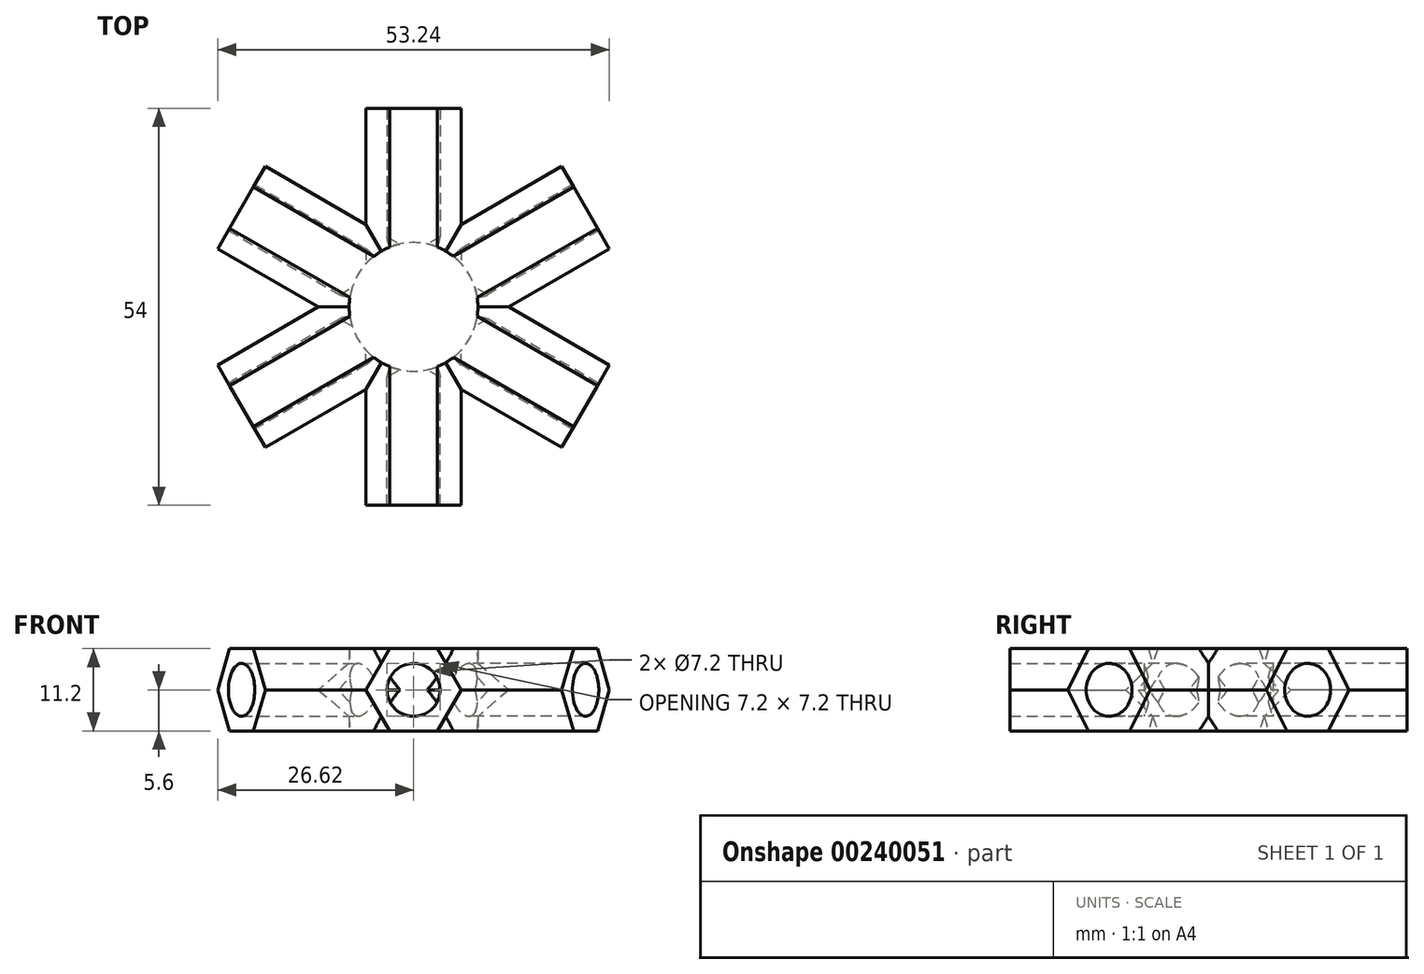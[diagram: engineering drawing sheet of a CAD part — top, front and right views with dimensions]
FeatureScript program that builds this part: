
annotation { "Feature Type Name" : "Feature", "Feature Type Description" : "" }
export const myFeature = defineFeature(function(context is Context, id is Id, definition is map)
    precondition{}
    {
        {
            var Q0;
            Q0=qCreatedBy(makeId("Front.planeOp"),FACE);
            var sketch = newSketch(context, id + "F0", { "sketchPlane" : qUnion([Q0])});
            skCircle(sketch, "E0", {"center": v(0, 0) * mm, "radius": 3.6 * mm});
            skLineSegment(sketch, "E1", {"start": v(0, 0) * mm, "end": v(0, 28.88) * mm, "construction": true});
            skLineSegment(sketch, "E2.0", {"start": v(3.23, -5.6) * mm, "end": v(-3.23, -5.6) * mm});
            skLineSegment(sketch, "E2.1", {"start": v(-3.23, -5.6) * mm, "end": v(-6.47, 0) * mm});
            skLineSegment(sketch, "E2.2", {"start": v(-6.47, 0) * mm, "end": v(-3.23, 5.6) * mm});
            skLineSegment(sketch, "E2.3", {"start": v(-3.23, 5.6) * mm, "end": v(3.23, 5.6) * mm});
            skLineSegment(sketch, "E2.4", {"start": v(3.23, 5.6) * mm, "end": v(6.47, 0) * mm});
            skLineSegment(sketch, "E2.5", {"start": v(6.47, 0) * mm, "end": v(3.23, -5.6) * mm});
            skPoint(sketch, "E2.0.midPoint", {"position": v(0, -5.6) * mm});
            skSolve(sketch);
        }
        {
            var Q0;
            Q0=makeQuery(id+"F0.imprint","IMPRINT",FACE,{"disambiguationData":[TD([[makeQuery(id+"F0.imprint","IMPRINT",EDGE,{"derivedFrom":sQuery(id+"F0.wireOp",EDGE,"E0")}),-1.0]])]});
            extrude(context, id + "F1", {"entities" : qUnion([Q0]), "depth" : 27 * mm});
        }
        {
            var Q0;
            Q0=makeQuery(id+"F1.opExtrude","SWEPT_BODY",BODY,{"disambiguationData":[OSD([sQuery(id+"F0.wireOp",EDGE,"E0"),sQuery(id+"F0.wireOp",EDGE,"0ab11b23-3792-4030-9bdc-7616e1c06152.0")])]});
            var Q1;
            Q1=sQuery(id+"F0.wireOp",EDGE,"E1");
            circularPattern(context, id + "F2", {"operationType" : NewBodyOperationType.ADD, "entities" : qUnion([Q0]), "axis" : qUnion([Q1]), "angle" : 360 * degree, "instanceCount" : 6, "equalSpace" : true});
        }
        {
            var Q0;
            Q0=qCreatedBy(makeId("Top.planeOp"),FACE);
            var sketch = newSketch(context, id + "F3", { "sketchPlane" : qUnion([Q0])});
            skCircle(sketch, "E3", {"center": v(0, 0) * mm, "radius": 8.75 * mm});
            skSolve(sketch);
        }
        {
            var Q0;
            Q0=makeQuery(id+"F3.imprint","IMPRINT",FACE,{"disambiguationData":[TD([[makeQuery(id+"F3.imprint","IMPRINT",EDGE,{"derivedFrom":sQuery(id+"F3.wireOp",EDGE,"E3")}),1.0]])]});
            var Q1;
            Q1=sQuery(id+"F3.wireOp",EDGE,"E3");
            extrude(context, id + "F4", {"entities" : qUnion([Q0]), "operationType" : NewBodyOperationType.ADD, "surfaceEntities" : qUnion([Q1]), "depth" : 5.6 * mm, "hasSecondDirection" : true, "secondDirectionOppositeDirection" : true, "secondDirectionDepth" : 5.6 * mm});
        }
    });
